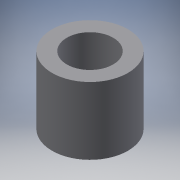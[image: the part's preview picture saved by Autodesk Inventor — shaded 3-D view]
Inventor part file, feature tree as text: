
AUTODESK INVENTOR PART (.ipt)
format: ipt  version: 2017 (Build 210142000, 142)  size: 94,720 bytes
history: native  units: mm
features: other x3, extrude x1, sketch x1, reference x1
ambient origin geometry x8: Origin, YZ Plane, XZ Plane, XY Plane, X Axis, Y Axis, Z Axis, Center Point
bodies: Solid1 (feature_tree)
feature tree (6):
  extrude  "Extrusion1"  Depth=8.0mm
  sketch  "Sketch1"  dims[d0=5.5mm d1=9.0mm d2=8.0mm d3=0.0mm]
  reference  "Reference1"
  parser-record x1  (decoder bookkeeping rows leaked as tree rows — omitted from the tree; the rows remain in map.json)
  other  "eLECTRONICS-ENCLOSURE.iam"
  other  "EE Base:1"
note: 1 file-system path scrubbed to <path> (originals preserved in map.json)
